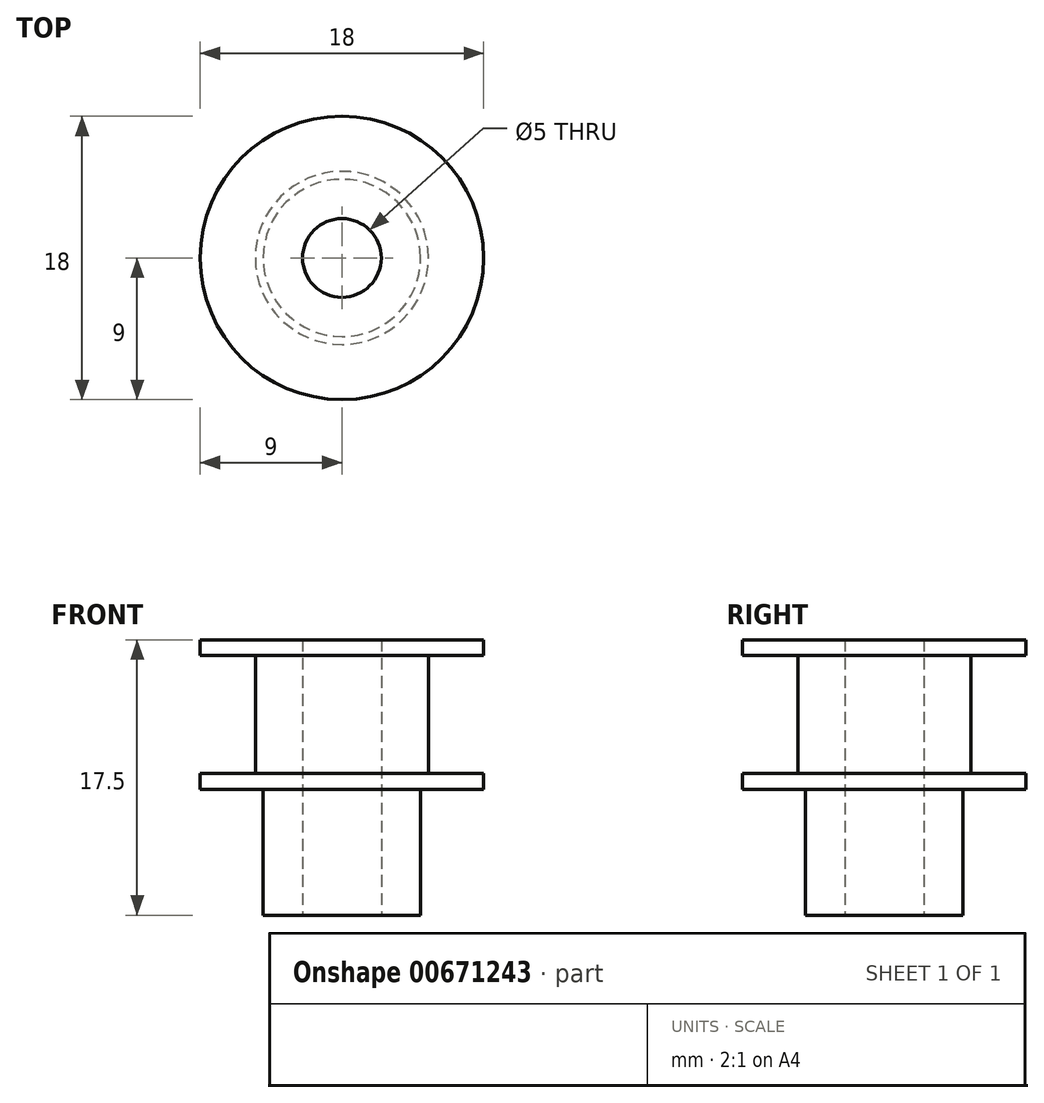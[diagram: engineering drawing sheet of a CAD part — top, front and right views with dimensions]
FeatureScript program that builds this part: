
annotation { "Feature Type Name" : "Feature", "Feature Type Description" : "" }
export const myFeature = defineFeature(function(context is Context, id is Id, definition is map)
    precondition{}
    {
        {
            var Q0;
            Q0=qCreatedBy(makeId("Front.planeOp"),FACE);
            var sketch = newSketch(context, id + "F0", { "sketchPlane" : qUnion([Q0])});
            skLineSegment(sketch, "E0", {"start": v(0, 0) * mm, "end": v(0, 17.5) * mm, "construction": true});
            skLineSegment(sketch, "E1.0", {"start": v(2.5, 0) * mm, "end": v(2.5, 17.5) * mm});
            skLineSegment(sketch, "E2", {"start": v(2.5, 0) * mm, "end": v(5, 0) * mm});
            skLineSegment(sketch, "E3", {"start": v(5, 0) * mm, "end": v(5, 8) * mm});
            skLineSegment(sketch, "E4", {"start": v(5, 8) * mm, "end": v(9, 8) * mm});
            skLineSegment(sketch, "E5", {"start": v(9, 8) * mm, "end": v(9, 9) * mm});
            skLineSegment(sketch, "E6", {"start": v(9, 9) * mm, "end": v(5.5, 9) * mm});
            skLineSegment(sketch, "E7", {"start": v(5.5, 9) * mm, "end": v(5.5, 16.5) * mm});
            skLineSegment(sketch, "E8", {"start": v(5.5, 16.5) * mm, "end": v(9, 16.5) * mm});
            skLineSegment(sketch, "E9", {"start": v(9, 16.5) * mm, "end": v(9, 17.5) * mm});
            skLineSegment(sketch, "E10", {"start": v(9, 17.5) * mm, "end": v(2.5, 17.5) * mm});
            skSolve(sketch);
        }
        {
            var Q0;
            Q0=makeQuery(id+"F0.imprint","IMPRINT",FACE,{"disambiguationData":[TD([[makeQuery(id+"F0.imprint","IMPRINT",EDGE,{"derivedFrom":sQuery(id+"F0.wireOp",EDGE,"E1.0")}),-1.0]])]});
            var Q1;
            Q1=sQuery(id+"F0.wireOp",EDGE,"E0");
            revolve(context, id + "F1", {"entities" : qUnion([Q0]), "axis" : qUnion([Q1]), "revolveType" : RevolveType.FULL});
        }
    });
